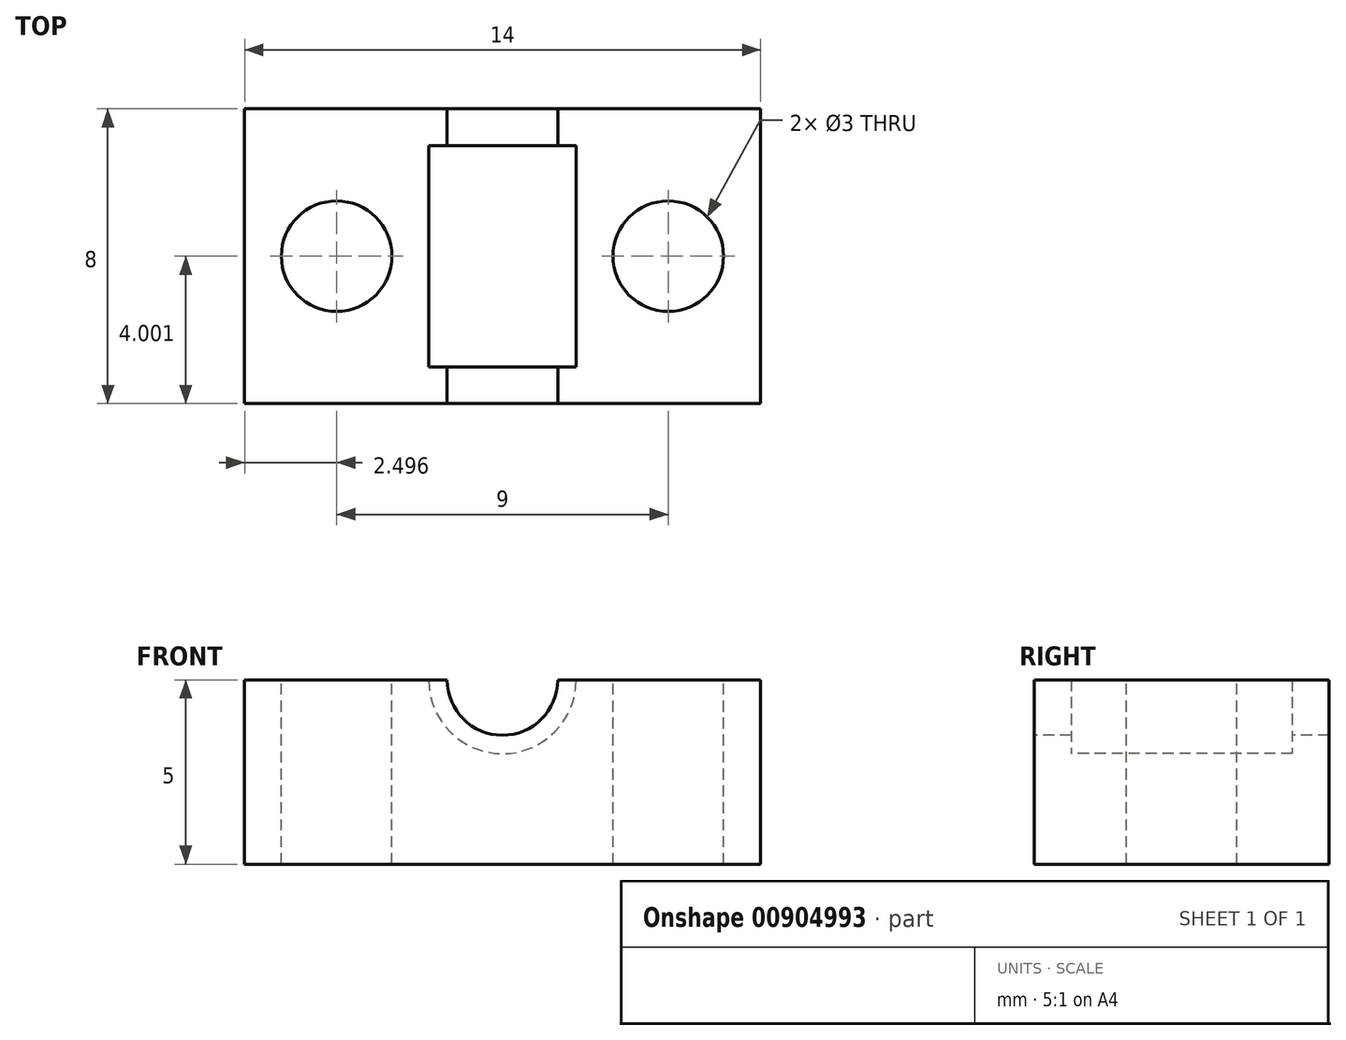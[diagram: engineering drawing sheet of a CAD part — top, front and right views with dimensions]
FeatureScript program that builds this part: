
annotation { "Feature Type Name" : "Feature", "Feature Type Description" : "" }
export const myFeature = defineFeature(function(context is Context, id is Id, definition is map)
    precondition{}
    {
        {
            var Q0;
            Q0=qCreatedBy(makeId("Top.planeOp"),FACE);
            var sketch = newSketch(context, id + "F0", { "sketchPlane" : qUnion([Q0])});
            skLineSegment(sketch, "E0.bottom", {"start": v(-12.4, -2.17) * mm, "end": v(1.6, -2.17) * mm});
            skLineSegment(sketch, "E0.top", {"start": v(-12.4, -10.17) * mm, "end": v(1.6, -10.17) * mm});
            skLineSegment(sketch, "E0.left", {"start": v(-12.4, -2.17) * mm, "end": v(-12.4, -10.17) * mm});
            skLineSegment(sketch, "E0.right", {"start": v(1.6, -2.17) * mm, "end": v(1.6, -10.17) * mm});
            skSolve(sketch);
        }
        {
            var Q0;
            Q0=qSketchRegion(id+"F0",true);
            extrude(context, id + "F1", {"entities" : qUnion([Q0]), "depth" : 5 * mm, "offsetDistance" : 25 * mm});
        }
        {
            var Q0;
            Q0=makeQuery(id+"F1.opExtrude","SWEPT_FACE",FACE,{"disambiguationData":[OSD([sQuery(id+"F0.wireOp",EDGE,"E0.top")])]});
            var sketch = newSketch(context, id + "F2", { "sketchPlane" : qUnion([Q0])});
            skCircle(sketch, "E1", {"center": v(-5.4, 5) * mm, "radius": 2 * mm});
            skSolve(sketch);
        }
        {
            var Q0;
            {var subQ0=sQuery(id+"F2.wireOp",EDGE,"E1");var subQ1=makeQuery(id+"F1.opExtrude","CAP_EDGE",EDGE,{"disambiguationData":[OSD([sQuery(id+"F0.wireOp",EDGE,"E0.top")])],"isStart":false});var subQ2=makeQuery(id+"F2.imprint","INTERSECT",VERTEX,{"disambiguationData":[OD(0.0)],"derivedFrom":[subQ1,subQ0]});Q0=makeQuery(id+"F2.imprint","IMPRINT",FACE,{"disambiguationData":[TD([[makeQuery(id+"F2.imprint","IMPRINT",EDGE,{"disambiguationData":[TD([[subQ2,1.0]])],"derivedFrom":subQ0}),1.0]])]});}
            var sketch = newSketch(context, id + "F3", { "sketchPlane" : qUnion([Q0])});
            skLineSegment(sketch, "E2.0.0", {"start": v(-7.4, 5) * mm, "end": v(-3.4, 5) * mm});
            skArc(sketch, "E2.0.1", {"start": v(-3.4, 5) * mm, "mid": v(-5.4, 7) * mm, "end": v(-7.4, 5) * mm});
            skCircle(sketch, "E3", {"center": v(-5.4, 5) * mm, "radius": 1.5 * mm});
            skSolve(sketch);
        }
        {
            var Q0;
            Q0=qSketchRegion(id+"F2",true);
            extrude(context, id + "F4", {"entities" : qUnion([Q0]), "operationType" : NewBodyOperationType.REMOVE, "oppositeDirection" : true, "depth" : 7 * mm, "offsetDistance" : 25 * mm, "hasSecondDirection" : true, "secondDirectionOppositeDirection" : false, "secondDirectionDepth" : -1 * mm});
        }
        {
            var Q0;
            Q0=qSketchRegion(id+"F3",true);
            extrude(context, id + "F5", {"entities" : qUnion([Q0]), "operationType" : NewBodyOperationType.REMOVE, "oppositeDirection" : true, "depth" : 25 * mm, "offsetDistance" : 25 * mm});
        }
        {
            var Q0;
            {var subQ1=sQuery(id+"F0.wireOp",EDGE,"E0.left");var subQ2=sQuery(id+"F0.wireOp",EDGE,"E0.top");var subQ3=sQuery(id+"F0.wireOp",EDGE,"E0.bottom");Q0=makeQuery(id+"F5.boolean.opBoolean","SPLIT",FACE,{"disambiguationData":[TD([makeQuery(id+"F1.opExtrude","SWEPT_FACE",FACE,{"disambiguationData":[OSD([subQ1])]})])],"derivedFrom":makeQuery(id+"F1.opExtrude","CAP_FACE",FACE,{"disambiguationData":[OSD([subQ3,subQ2,subQ1,sQuery(id+"F0.wireOp",EDGE,"E0.right")])],"isStart":false})});}
            var sketch = newSketch(context, id + "F6", { "sketchPlane" : qUnion([Q0])});
            skLineSegment(sketch, "E4", {"start": v(-7.4, -6.17) * mm, "end": v(-12.4, -6.17) * mm});
            skCircle(sketch, "E5", {"center": v(-9.9, -6.17) * mm, "radius": 1.5 * mm});
            skLineSegment(sketch, "E6.0", {"start": v(1.6, -2.17) * mm, "end": v(1.6, -10.17) * mm});
            skPoint(sketch, "E7", {"position": v(1.6, -6.17) * mm});
            skLineSegment(sketch, "E8", {"start": v(-12.4, -6.17) * mm, "end": v(1.6, -6.17) * mm});
            skLineSegment(sketch, "E9", {"start": v(-5.4, -6.17) * mm, "end": v(-5.4, -7.51) * mm});
            skLineSegment(sketch, "E10", {"start": v(-5.4, -7.51) * mm, "end": v(-5.4, -6.17) * mm});
            skCircle(sketch, "E11.MirrorC", {"center": v(-0.9, -6.17) * mm, "radius": 1.5 * mm});
            skSolve(sketch);
        }
        {
            var Q0;
            Q0=qSketchRegion(id+"F6",true);
            extrude(context, id + "F7", {"entities" : qUnion([Q0]), "operationType" : NewBodyOperationType.REMOVE, "oppositeDirection" : true, "depth" : 5 * mm, "offsetDistance" : 25 * mm});
        }
    });
